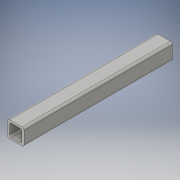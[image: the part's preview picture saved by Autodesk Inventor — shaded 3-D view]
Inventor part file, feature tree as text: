
AUTODESK INVENTOR PART (.ipt)
format: ipt  version: 2016 (Build 200138000, 138)  size: 113,664 bytes
history: native  units: in
note: dims shown in document units (in); Inventor stores cm internally (conversion verified against a paired STEP export)
features: extrude x1, sketch x1
ambient origin geometry x8: Origin, YZ Plane, XZ Plane, XY Plane, X Axis, Y Axis, Z Axis, Center Point
bodies: Solid1 (feature_tree)
feature tree (2):
  extrude  "Extrusion1"  Depth=1.0in
  sketch  "Sketch1"  dims[d0=1.0in d1=1.0in d2=0.125in d3=0.125in d4=9.0in d5=0.0in]
